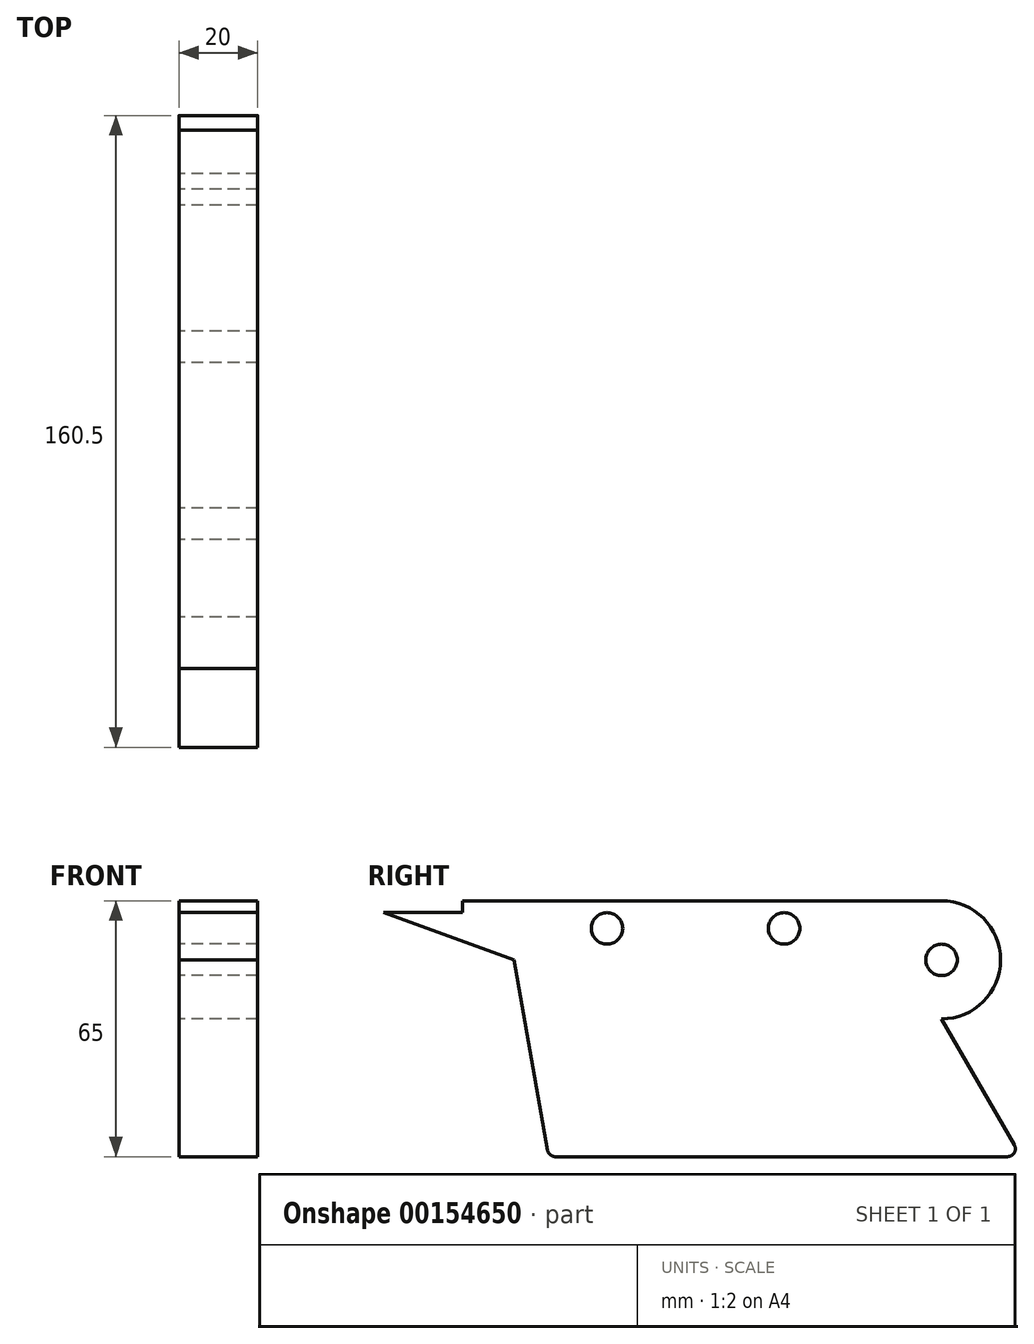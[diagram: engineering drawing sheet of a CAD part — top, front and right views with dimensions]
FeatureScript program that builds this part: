
annotation { "Feature Type Name" : "Feature", "Feature Type Description" : "" }
export const myFeature = defineFeature(function(context is Context, id is Id, definition is map)
    precondition{}
    {
        {
            var Q0;
            Q0=qCreatedBy(makeId("Right.planeOp"),FACE);
            var sketch = newSketch(context, id + "F0", { "sketchPlane" : qUnion([Q0])});
            skLineSegment(sketch, "E0.bottom", {"start": v(-71.76, 15) * mm, "end": v(50, 15) * mm});
            skArc(sketch, "E1", {"start": v(50, -15) * mm, "mid": v(65, 0) * mm, "end": v(50, 15) * mm});
            skLineSegment(sketch, "E2", {"start": v(-91.76, 12) * mm, "end": v(-58.6, -0.07) * mm});
            skCircle(sketch, "E3", {"center": v(50, 0) * mm, "radius": 4 * mm});
            skPoint(sketch, "E4.visualSharp", {"position": v(-17.58, -15) * mm});
            skPoint(sketch, "E5.visualSharp", {"position": v(-100, 15) * mm});
            skCircle(sketch, "E6", {"center": v(10, 8) * mm, "radius": 4 * mm});
            skCircle(sketch, "E7", {"center": v(-35, 8) * mm, "radius": 4 * mm});
            skLineSegment(sketch, "E8", {"start": v(50, -15) * mm, "end": v(68.48, -47) * mm});
            skLineSegment(sketch, "E9", {"start": v(66.74, -50) * mm, "end": v(-48.11, -50) * mm});
            skLineSegment(sketch, "E10", {"start": v(-50.08, -48.35) * mm, "end": v(-58.6, -0.07) * mm});
            skPoint(sketch, "E11.visualSharp", {"position": v(70.2, -50) * mm});
            skArc(sketch, "E11.filletArc", {"start": v(66.74, -50) * mm, "mid": v(68.48, -49) * mm, "end": v(68.48, -47) * mm});
            skPoint(sketch, "E12.visualSharp", {"position": v(-49.8, -50) * mm});
            skArc(sketch, "E12.filletArc", {"start": v(-50.08, -48.35) * mm, "mid": v(-49.4, -49.53) * mm, "end": v(-48.11, -50) * mm});
            skLineSegment(sketch, "E13.top", {"start": v(-71.76, 12) * mm, "end": v(-91.76, 12) * mm});
            skLineSegment(sketch, "E13.left", {"start": v(-71.76, 15) * mm, "end": v(-71.76, 12) * mm});
            skSolve(sketch);
        }
        {
            var Q0;
            Q0 = qSketchRegion(id + "F0", true);
            extrude(context, id + "F1", {"entities" : qUnion([Q0]), "depth" : 20 * mm});
        }
    });
